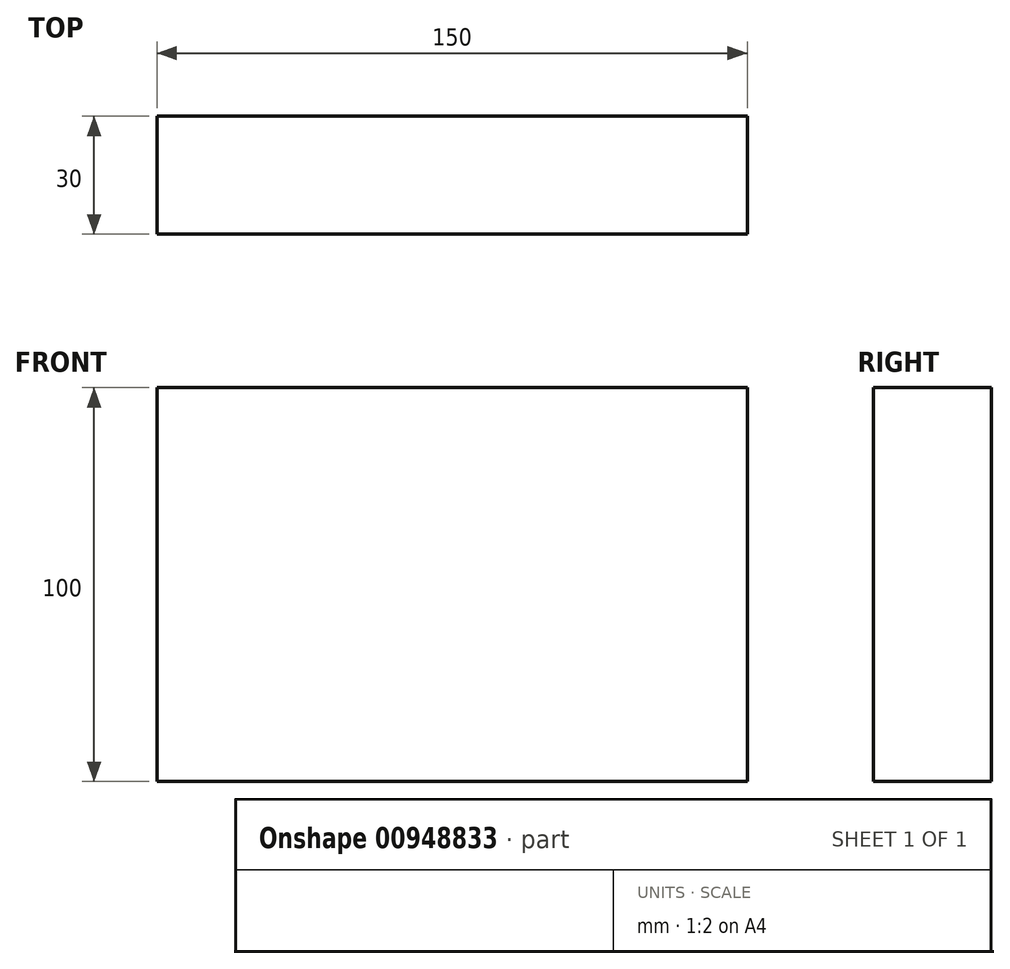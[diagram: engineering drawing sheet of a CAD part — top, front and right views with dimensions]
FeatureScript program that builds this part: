
annotation { "Feature Type Name" : "Feature", "Feature Type Description" : "" }
export const myFeature = defineFeature(function(context is Context, id is Id, definition is map)
    precondition{}
    {
        {
            var Q0;
            Q0=qCreatedBy(makeId("Front.planeOp"),FACE);
            var sketch = newSketch(context, id + "F0", { "sketchPlane" : qUnion([Q0])});
            skLineSegment(sketch, "E0.bottom", {"start": v(75, -50) * mm, "end": v(-75, -50) * mm});
            skLineSegment(sketch, "E0.top", {"start": v(75, 50) * mm, "end": v(-75, 50) * mm});
            skLineSegment(sketch, "E0.left", {"start": v(75, -50) * mm, "end": v(75, 50) * mm});
            skLineSegment(sketch, "E0.right", {"start": v(-75, -50) * mm, "end": v(-75, 50) * mm});
            skPoint(sketch, "E0.middle", {"position": v(0, 0) * mm});
            skSolve(sketch);
        }
        {
            var Q0;
            Q0=qSketchRegion(id+"F0",true);
            extrude(context, id + "F1", {"entities" : qUnion([Q0]), "depth" : 30 * mm, "offsetDistance" : 25 * mm});
        }
    });
